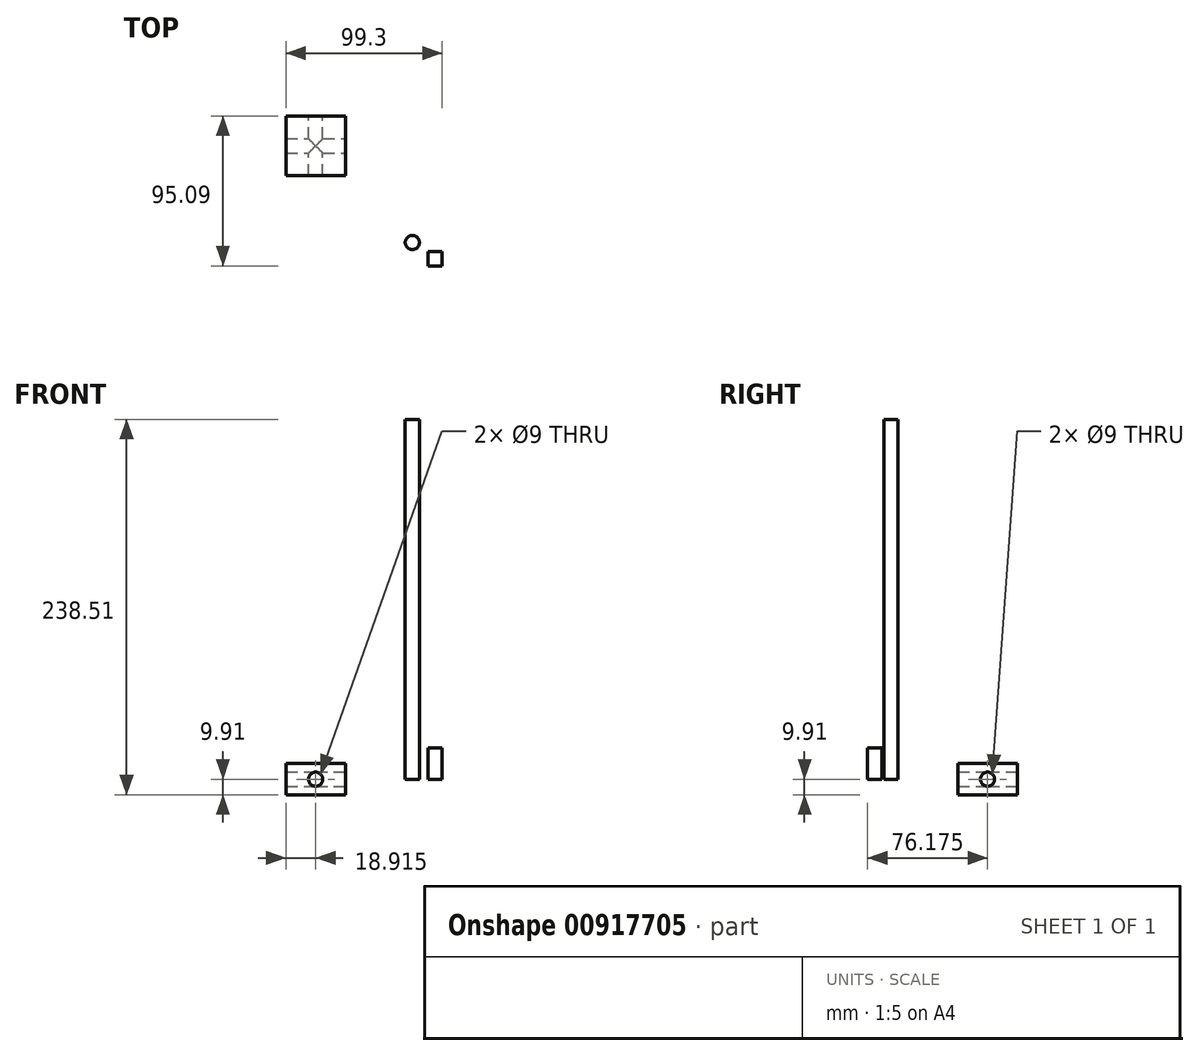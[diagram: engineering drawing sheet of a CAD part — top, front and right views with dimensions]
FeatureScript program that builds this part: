
annotation { "Feature Type Name" : "Feature", "Feature Type Description" : "" }
export const myFeature = defineFeature(function(context is Context, id is Id, definition is map)
    precondition{}
    {
        {
            var Q0;
            Q0=qCreatedBy(makeId("Top.planeOp"),FACE);
            var sketch = newSketch(context, id + "F0", { "sketchPlane" : qUnion([Q0])});
            skLineSegment(sketch, "E0", {"start": v(0, 0) * mm, "end": v(-37.83, 0) * mm});
            skLineSegment(sketch, "E1", {"start": v(-37.83, 0) * mm, "end": v(-37.83, 37.83) * mm});
            skLineSegment(sketch, "E2", {"start": v(0, 37.83) * mm, "end": v(-37.83, 37.83) * mm});
            skLineSegment(sketch, "E3", {"start": v(0, 0) * mm, "end": v(0, 37.83) * mm});
            skSolve(sketch);
        }
        {
            var Q0;
            Q0 = qSketchRegion(id + "F0", true);
            extrude(context, id + "F1", {"entities" : qUnion([Q0]), "endBound" : BoundingType.SYMMETRIC, "depth" : 19.8 * mm, "offsetDistance" : 25.4 * mm});
        }
        {
            var Q0;
            Q0=makeQuery(id+"F1.opExtrude","SWEPT_FACE",FACE,{"disambiguationData":[OSD([sQuery(id+"F0.wireOp",EDGE,"E2")])]});
            var sketch = newSketch(context, id + "F2", { "sketchPlane" : qUnion([Q0])});
            skLineSegment(sketch, "E4", {"start": v(37.83, 9.9) * mm, "end": v(37.83, -9.9) * mm});
            skLineSegment(sketch, "E5", {"start": v(37.83, -9.9) * mm, "end": v(0, -9.9) * mm});
            skLineSegment(sketch, "E6", {"start": v(0, -9.9) * mm, "end": v(0, 9.9) * mm});
            skLineSegment(sketch, "E7", {"start": v(0, 9.9) * mm, "end": v(37.83, 9.9) * mm});
            skPoint(sketch, "E8", {"position": v(18.91, 0) * mm});
            skPoint(sketch, "E8.positionSnap0", {"position": v(18.91, 9.9) * mm});
            skPoint(sketch, "E8.positionSnap1", {"position": v(37.83, 0) * mm});
            skSolve(sketch);
        }
        {
            var Q0;
            Q0=makeQuery(id+"F1.opExtrude","SWEPT_FACE",FACE,{"disambiguationData":[OSD([sQuery(id+"F0.wireOp",EDGE,"E1")])]});
            var sketch = newSketch(context, id + "F3", { "sketchPlane" : qUnion([Q0])});
            skPoint(sketch, "E9", {"position": v(-18.91, 0) * mm});
            skPoint(sketch, "E9.positionSnap0", {"position": v(0, 0) * mm});
            skPoint(sketch, "E9.positionSnap1", {"position": v(-18.91, 9.9) * mm});
            skSolve(sketch);
        }
        {
            var Q0;
            Q0=makeQuery(id+"F1.opExtrude","SWEPT_FACE",FACE,{"disambiguationData":[OSD([sQuery(id+"F0.wireOp",EDGE,"E0")])]});
            var sketch = newSketch(context, id + "F4", { "sketchPlane" : qUnion([Q0])});
            skPoint(sketch, "E10", {"position": v(-18.91, 0) * mm});
            skPoint(sketch, "E10.positionSnap0", {"position": v(0, 0) * mm});
            skPoint(sketch, "E10.positionSnap1", {"position": v(-18.91, 9.9) * mm});
            skSolve(sketch);
        }
        {
            var Q0;
            Q0=makeQuery(id+"F1.opExtrude","SWEPT_FACE",FACE,{"disambiguationData":[OSD([sQuery(id+"F0.wireOp",EDGE,"E3")])]});
            var sketch = newSketch(context, id + "F5", { "sketchPlane" : qUnion([Q0])});
            skPoint(sketch, "E11", {"position": v(18.91, 0) * mm});
            skPoint(sketch, "E11.positionSnap0", {"position": v(37.83, 0) * mm});
            skPoint(sketch, "E11.positionSnap1", {"position": v(18.91, 9.9) * mm});
            skSolve(sketch);
        }
        {
            var Q0;
            Q0=sQuery(id+"F5.wireOp",VERTEX,"E11");
            var Q1;
            Q1=sQuery(id+"F3.wireOp",VERTEX,"E9");
            var Q2;
            Q2=makeQuery(id+"F1.opExtrude","SWEPT_BODY",BODY,{"disambiguationData":[OSD([sQuery(id+"F0.wireOp",EDGE,"E0"),sQuery(id+"F0.wireOp",EDGE,"E1"),sQuery(id+"F0.wireOp",EDGE,"E2"),sQuery(id+"F0.wireOp",EDGE,"E3")])]});
            hole(context, id + "F6", {"style" : HoleStyle.SIMPLE, "endStyle" : HoleEndStyle.THROUGH, "holeDiameter" : 9 * mm, "majorDiameter" : 6.35 * mm, "isTappedThrough" : true, "tappedDepth" : 12.7 * mm, "tapClearance" : 3, "locations" : qUnion([Q0, Q1]), "scope" : qUnion([Q2])});
        }
        {
            var Q0;
            Q0=sQuery(id+"F2.wireOp",VERTEX,"E8");
            var Q1;
            Q1=sQuery(id+"F4.wireOp",VERTEX,"E10");
            var Q2;
            Q2=makeQuery(id+"F1.opExtrude","SWEPT_BODY",BODY,{"disambiguationData":[OSD([sQuery(id+"F0.wireOp",EDGE,"E0"),sQuery(id+"F0.wireOp",EDGE,"E1"),sQuery(id+"F0.wireOp",EDGE,"E2"),sQuery(id+"F0.wireOp",EDGE,"E3")])]});
            hole(context, id + "F7", {"style" : HoleStyle.SIMPLE, "endStyle" : HoleEndStyle.THROUGH, "holeDiameter" : 9 * mm, "majorDiameter" : 6.35 * mm, "isTappedThrough" : true, "tappedDepth" : 12.7 * mm, "tapClearance" : 3, "locations" : qUnion([Q0, Q1]), "scope" : qUnion([Q2])});
        }
        {
            var Q0;
            Q0=qCreatedBy(makeId("Top.planeOp"),FACE);
            var sketch = newSketch(context, id + "F8", { "sketchPlane" : qUnion([Q0])});
            skCircle(sketch, "E12.0", {"center": v(42.5, -42.42) * mm, "radius": 4.5 * mm});
            skSolve(sketch);
        }
        {
            var Q0;
            Q0 = qSketchRegion(id + "F8", true);
            extrude(context, id + "F9", {"entities" : qUnion([Q0]), "depth" : 228.6 * mm, "offsetDistance" : 25.4 * mm});
        }
        {
            var Q0;
            Q0=qCreatedBy(makeId("Top.planeOp"),FACE);
            var sketch = newSketch(context, id + "F10", { "sketchPlane" : qUnion([Q0])});
            skLineSegment(sketch, "E13", {"start": v(52.47, -57.26) * mm, "end": v(52.47, -48.26) * mm});
            skLineSegment(sketch, "E14", {"start": v(52.47, -48.26) * mm, "end": v(61.47, -48.26) * mm});
            skLineSegment(sketch, "E15", {"start": v(61.47, -57.26) * mm, "end": v(61.47, -48.26) * mm});
            skLineSegment(sketch, "E16", {"start": v(52.47, -57.26) * mm, "end": v(61.47, -57.26) * mm});
            skSolve(sketch);
        }
        {
            var Q0;
            Q0 = qSketchRegion(id + "F10", true);
            extrude(context, id + "F11", {"entities" : qUnion([Q0]), "depth" : 19.8 * mm, "offsetDistance" : 25.4 * mm});
        }
    });
